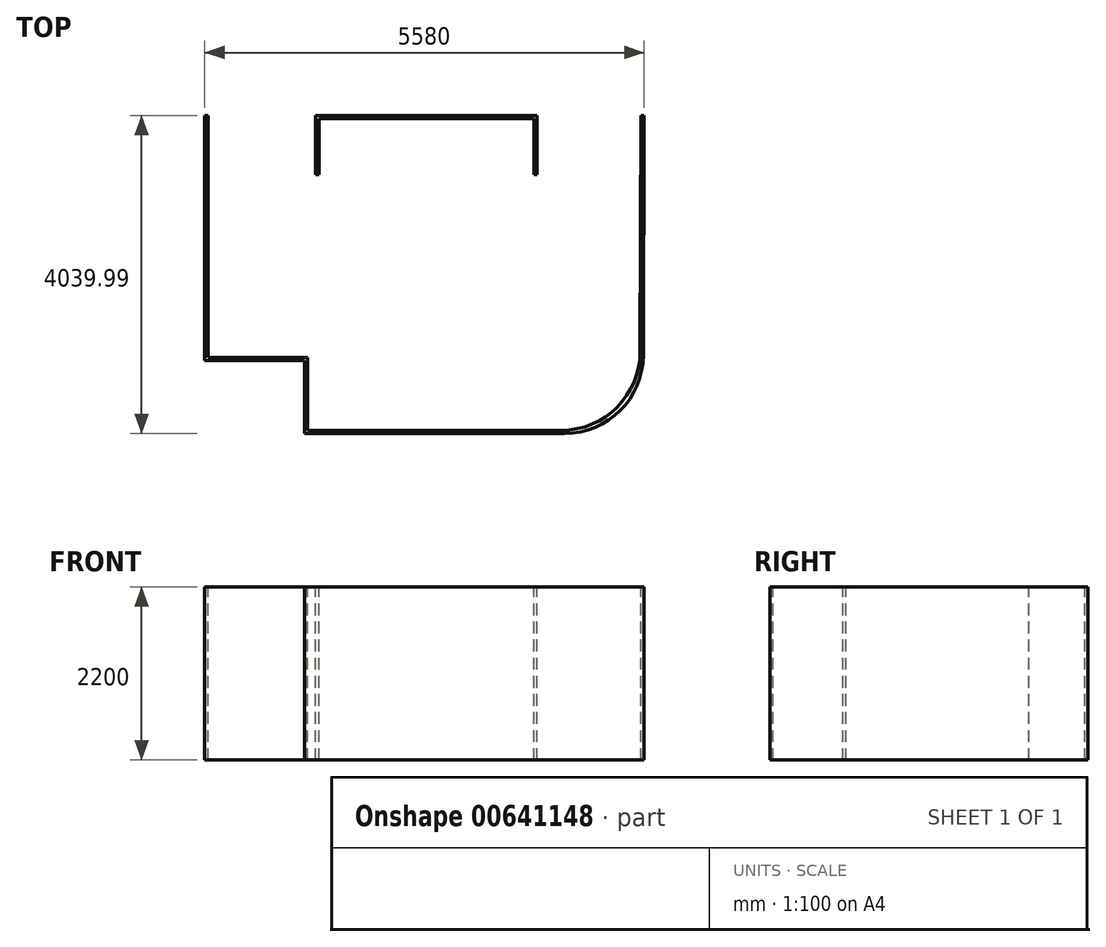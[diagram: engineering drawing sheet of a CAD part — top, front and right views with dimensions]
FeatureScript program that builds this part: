
annotation { "Feature Type Name" : "Feature", "Feature Type Description" : "" }
export const myFeature = defineFeature(function(context is Context, id is Id, definition is map)
    precondition{}
    {
        {
            var Q0;
            Q0=qCreatedBy(makeId("Top.planeOp"),FACE);
            var sketch = newSketch(context, id + "F0", { "sketchPlane" : qUnion([Q0])});
            skLineSegment(sketch, "E0", {"start": v(2858.04, 1802.38) * mm, "end": v(2849.79, -1200.36) * mm});
            skLineSegment(sketch, "E1", {"start": v(1849.79, -2197.6) * mm, "end": v(-1375.96, -2197.6) * mm});
            skLineSegment(sketch, "E2", {"start": v(-1375.96, -2197.6) * mm, "end": v(-1375.96, -1272.6) * mm});
            skLineSegment(sketch, "E3", {"start": v(-1375.96, -1272.6) * mm, "end": v(-2641.96, -1272.6) * mm});
            skLineSegment(sketch, "E4", {"start": v(-2641.96, -1272.6) * mm, "end": v(-2641.96, 1801.76) * mm});
            skLineSegment(sketch, "E5", {"start": v(1541.22, 1801.76) * mm, "end": v(1541.22, 1051.76) * mm});
            skLineSegment(sketch, "E6", {"start": v(-1271.96, 1801.76) * mm, "end": v(-1271.96, 1051.76) * mm});
            skLineSegment(sketch, "E7", {"start": v(-1271.96, 1801.76) * mm, "end": v(1541.22, 1801.76) * mm});
            skLineSegment(sketch, "E8.0", {"start": v(-2681.96, -1312.6) * mm, "end": v(-2681.96, 1801.76) * mm});
            skLineSegment(sketch, "E8.1", {"start": v(2898.04, 1802.27) * mm, "end": v(2889.68, -1240.36) * mm});
            skLineSegment(sketch, "E8.2", {"start": v(1889.68, -2237.6) * mm, "end": v(-1415.96, -2237.6) * mm});
            skLineSegment(sketch, "E8.3", {"start": v(-1415.96, -2237.6) * mm, "end": v(-1415.96, -1312.6) * mm});
            skLineSegment(sketch, "E8.4", {"start": v(-1415.96, -1312.6) * mm, "end": v(-2681.96, -1312.6) * mm});
            skPoint(sketch, "E9.visualSharp", {"position": v(2847.04, -2197.6) * mm});
            skArc(sketch, "E9.filletArc", {"start": v(1849.79, -2197.6) * mm, "mid": v(2555.92, -1905.68) * mm, "end": v(2849.79, -1200.36) * mm});
            skPoint(sketch, "E10.visualSharp", {"position": v(2886.93, -2237.6) * mm});
            skArc(sketch, "E10.filletArc", {"start": v(1889.68, -2237.6) * mm, "mid": v(2595.81, -1945.68) * mm, "end": v(2889.68, -1240.36) * mm});
            skLineSegment(sketch, "E11", {"start": v(-2681.96, 1801.76) * mm, "end": v(-2641.96, 1801.76) * mm});
            skLineSegment(sketch, "E12", {"start": v(2858.04, 1802.38) * mm, "end": v(2898.04, 1802.27) * mm});
            skLineSegment(sketch, "E13", {"start": v(-1271.96, 1051.76) * mm, "end": v(-1231.96, 1051.76) * mm});
            skLineSegment(sketch, "E14", {"start": v(-1231.96, 1051.76) * mm, "end": v(-1231.96, 1761.76) * mm});
            skLineSegment(sketch, "E15", {"start": v(-1231.96, 1761.76) * mm, "end": v(1501.22, 1761.76) * mm});
            skLineSegment(sketch, "E16", {"start": v(1501.22, 1761.76) * mm, "end": v(1501.22, 1051.76) * mm});
            skLineSegment(sketch, "E17", {"start": v(1501.22, 1051.76) * mm, "end": v(1541.22, 1051.76) * mm});
            skSolve(sketch);
        }
        {
            var Q0;
            Q0=makeQuery(id+"F0.imprint","IMPRINT",FACE,{"disambiguationData":[TD([[makeQuery(id+"F0.imprint","IMPRINT",EDGE,{"derivedFrom":sQuery(id+"F0.wireOp",EDGE,"E0")}),1.0]])]});
            var Q1;
            Q1=makeQuery(id+"F0.imprint","IMPRINT",FACE,{"disambiguationData":[TD([[makeQuery(id+"F0.imprint","IMPRINT",EDGE,{"derivedFrom":sQuery(id+"F0.wireOp",EDGE,"E5")}),-1.0]])]});
            extrude(context, id + "F1", {"entities" : qUnion([Q0, Q1]), "oppositeDirection" : true, "depth" : 2200 * mm, "offsetDistance" : 25 * mm});
        }
    });
